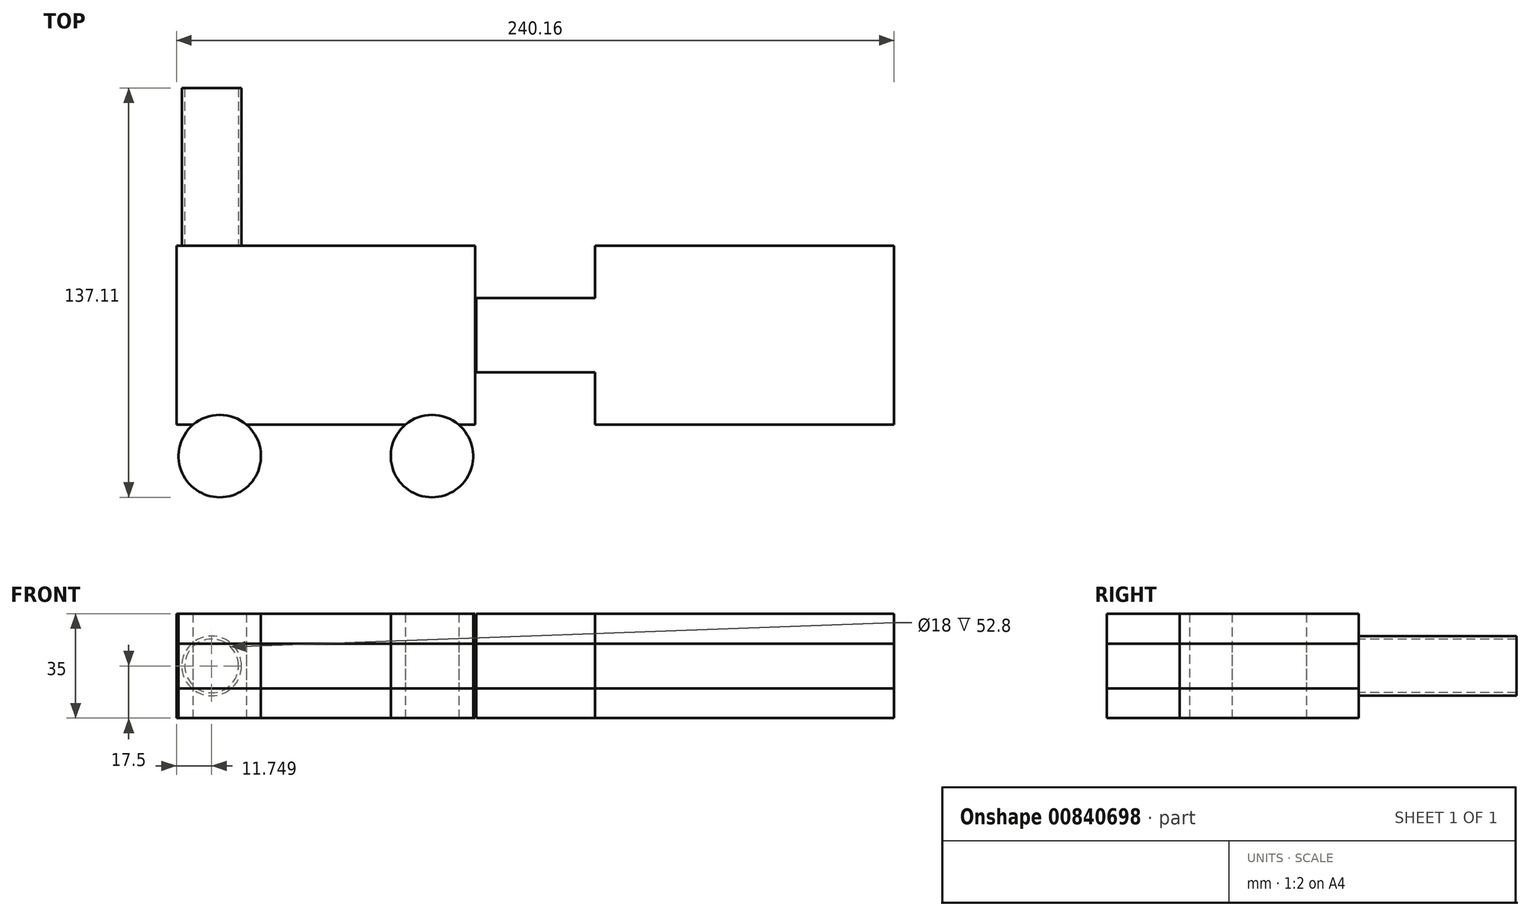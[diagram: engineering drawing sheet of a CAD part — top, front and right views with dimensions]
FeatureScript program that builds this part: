
annotation { "Feature Type Name" : "Feature", "Feature Type Description" : "" }
export const myFeature = defineFeature(function(context is Context, id is Id, definition is map)
    precondition{}
    {
        {
            var Q0;
            Q0=qCreatedBy(makeId("Top.planeOp"),FACE);
            var sketch = newSketch(context, id + "F0", { "sketchPlane" : qUnion([Q0])});
            skLineSegment(sketch, "E0.bottom", {"start": v(50, 30) * mm, "end": v(-50, 30) * mm});
            skLineSegment(sketch, "E0.top", {"start": v(50, -30) * mm, "end": v(-50, -30) * mm});
            skLineSegment(sketch, "E0.left", {"start": v(50, 30) * mm, "end": v(50, -30) * mm});
            skLineSegment(sketch, "E0.right", {"start": v(-50, 30) * mm, "end": v(-50, -30) * mm});
            skPoint(sketch, "E0.middle", {"position": v(0, 0) * mm});
            skCircle(sketch, "E1", {"center": v(-35.52, -40.5) * mm, "radius": 13.8 * mm});
            skCircle(sketch, "E2.MirrorC", {"center": v(35.52, -40.5) * mm, "radius": 13.8 * mm});
            skLineSegment(sketch, "E3.bottom", {"start": v(100.32, 12.5) * mm, "end": v(50.32, 12.5) * mm});
            skLineSegment(sketch, "E3.top", {"start": v(100.32, -12.5) * mm, "end": v(50.32, -12.5) * mm});
            skLineSegment(sketch, "E3.left", {"start": v(100.32, 12.5) * mm, "end": v(100.32, -12.5) * mm});
            skLineSegment(sketch, "E3.right", {"start": v(50.32, 12.5) * mm, "end": v(50.32, -12.5) * mm});
            skPoint(sketch, "E3.middle", {"position": v(75.32, 0) * mm});
            skLineSegment(sketch, "E4.bottom", {"start": v(90.16, 30) * mm, "end": v(190.16, 30) * mm});
            skLineSegment(sketch, "E4.top", {"start": v(90.16, -30) * mm, "end": v(190.16, -30) * mm});
            skLineSegment(sketch, "E4.left", {"start": v(90.16, 30) * mm, "end": v(90.16, -30) * mm});
            skLineSegment(sketch, "E4.right", {"start": v(190.16, 30) * mm, "end": v(190.16, -30) * mm});
            skPoint(sketch, "E4.middle", {"position": v(140.16, 0) * mm});
            skSolve(sketch);
        }
        {
            var Q0;
            Q0=makeQuery(id+"F0.imprint","IMPRINT",FACE,{"disambiguationData":[TD([[makeQuery(id+"F0.imprint","IMPRINT",EDGE,{"derivedFrom":sQuery(id+"F0.wireOp",EDGE,"E0.bottom")}),1.0]])]});
            extrude(context, id + "F1", {"entities" : qUnion([Q0]), "endBound" : BoundingType.SYMMETRIC, "depth" : 35 * mm, "offsetDistance" : 25 * mm});
        }
        {
            var Q0;
            Q0=makeQuery(id+"F1.opExtrude","SWEPT_FACE",FACE,{"disambiguationData":[OSD([sQuery(id+"F0.wireOp",EDGE,"E0.bottom")])]});
            var sketch = newSketch(context, id + "F2", { "sketchPlane" : qUnion([Q0])});
            skCircle(sketch, "E5", {"center": v(38.25, 0) * mm, "radius": 10 * mm});
            skCircle(sketch, "E6", {"center": v(38.25, 0) * mm, "radius": 9 * mm});
            skSolve(sketch);
        }
        {
            var Q0;
            Q0 = qSketchRegion(id + "F2", true);
            extrude(context, id + "F3", {"entities" : qUnion([Q0]), "operationType" : NewBodyOperationType.ADD, "depth" : 52.8 * mm, "offsetDistance" : 25 * mm});
        }
        {
            var Q0;
            Q0 = qSketchRegion(id + "F0", true);
            extrude(context, id + "F4", {"entities" : qUnion([Q0]), "endBound" : BoundingType.SYMMETRIC, "depth" : 15 * mm, "offsetDistance" : 25 * mm});
        }
        {
            var Q0;
            Q0 = qSketchRegion(id + "F0", true);
            extrude(context, id + "F5", {"entities" : qUnion([Q0]), "endBound" : BoundingType.SYMMETRIC, "depth" : 35 * mm, "offsetDistance" : 25 * mm});
        }
    });
